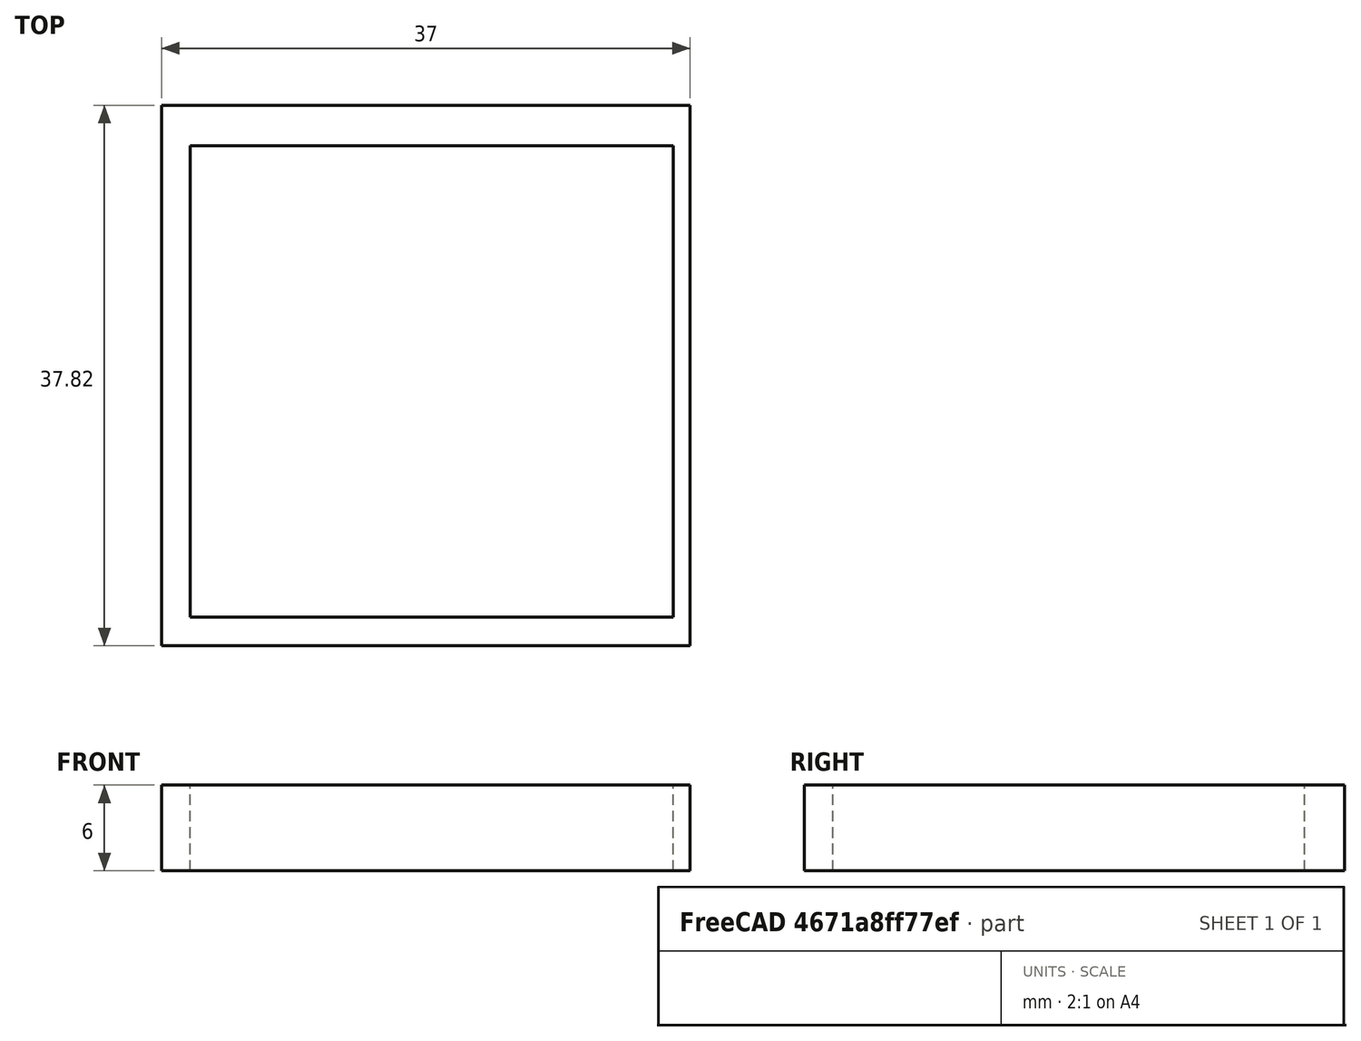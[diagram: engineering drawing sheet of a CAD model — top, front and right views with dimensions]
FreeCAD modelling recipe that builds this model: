
FCSTD DOCUMENT  (FreeCAD 0.18.4R)
Label: midi_pad_square_mount_2
License: All rights reserved
LicenseURL: http://en.wikipedia.org/wiki/All_rights_reserved
objects: Path::FeaturePython×13, Sketcher::SketchObject×8, App::MeasureDistance×5, Mesh::FeaturePython×5, PartDesign::Pocket×4, Part::FeaturePython×4, PartDesign::Hole×2, App::FeaturePython×2, App::DocumentObjectGroup×2, Path::FeatureCompoundPython×2, PartDesign::Pad×1, Spreadsheet::Sheet×1, Image::ImagePlane×1, PartDesign::Fillet×1, PartDesign::Body×1
note: 32 computed .brp shape members not serialized (recipe doc carries the construction recipe); baked Part::Feature solids carry a one-line shape summary decoded from their .brp

FEATURE [Sketcher::SketchObject] Sketch  label="base"
  MapMode = 5
  Support = -> [XY_Plane]
  sketch-geometry (4):
    g0: LineSegment StartX=-11.5 StartY=11.91 StartZ=0 EndX=11.5 EndY=11.91 EndZ=0
    g1: LineSegment StartX=11.5 StartY=11.91 StartZ=0 EndX=11.5 EndY=-11.91 EndZ=0
    g2: LineSegment StartX=11.5 StartY=-11.91 StartZ=0 EndX=-11.5 EndY=-11.91 EndZ=0
    g3: LineSegment StartX=-11.5 StartY=-11.91 StartZ=0 EndX=-11.5 EndY=11.91 EndZ=0
  constraints (11):
    c: Coincident(g0,g1)
    c: Coincident(g1,g2)
    c: Coincident(g2,g3)
    c: Coincident(g3,g0)
    c: Horizontal(g0)
    c: Horizontal(g2)
    c: Vertical(g1)
    c: Vertical(g3)
    c: DistanceY(g1,g1) = 23.82
    c: DistanceX(g0,g0) = 23
    c: Symmetric(g0,g2,g-1)
FEATURE [PartDesign::Pad] Pad  label="basePlate"
  Length = 6
  Length2 = 100
  Profile = -> Sketch
  Type = 0
  expr: Length = parameters.separator + parameters.balero_h
FEATURE [Spreadsheet::Sheet] Spreadsheet  label="parameters"
  cells = A1=balero_R; B1(balero_R)=7.95; A2=balero_r; B2(balero_r)=2.35; A3=balero_h; B3(balero_h)=5; A4=pin_w; B4(pin_w)=10.2; A5=r_w; B5(r_w)=10; A6=cutout_d; B6(cutout_d)=1.7; A7=wall_thickness; B7(wall_thickness)=3.5; A8=separator; B8(separator)=1; A9=center hole D; B9(center_hole_D)=3; A10=screw Head D; B10(screwHeadD)=5.5; A11=screw D; B11(screwMountD)=3.5; A12=OpToolHeightStep; B12(OpToolHeightStep)=0.25
FEATURE [Image::ImagePlane] ImagePlane
  Placement = pos=(99.4,-140.15,0) rot=(0,0,1;0rad)
  XSize = 222.326
  YSize = 305.698
FEATURE [App::MeasureDistance] Distance  label="Distance: left to center"
  Distance = 11.5
  P1 = (-11.5,0,0)
  P2 = (0,0,0)
FEATURE [App::MeasureDistance] Distance001  label="Distance: right to center"
  Distance = 11.5
  P1 = (11.5,0,0)
  P2 = (0,0,0)
FEATURE [App::MeasureDistance] Distance002  label="Distance: bottom to center"
  Distance = 7.58
  P1 = (0,-7.58,0)
  P2 = (0,0,0)
FEATURE [App::MeasureDistance] Distance003  label="Distance: up to center"
  Distance = 7.56
  P1 = (0,7.56,0)
  P2 = (0,0,0)
FEATURE [Sketcher::SketchObject] Sketch001  label="balero+wall"
  MapMode = 5
  Placement = pos=(0,0,6) rot=(0,0,1;0rad)
  Support = -> [Pad]
  expr: Constraints[1] = parameters.balero_R + parameters.wall_thickness
  sketch-geometry (5):
    g0: Circle CenterX=0 CenterY=0 CenterZ=0 NormalX=0 NormalY=0 NormalZ=1 AngleXU=0 Radius=11.45
    g1: LineSegment StartX=-20 StartY=20 StartZ=0 EndX=20 EndY=20 EndZ=0
    g2: LineSegment StartX=20 StartY=20 StartZ=0 EndX=20 EndY=-20 EndZ=0
    g3: LineSegment StartX=20 StartY=-20 StartZ=0 EndX=-20 EndY=-20 EndZ=0
    g4: LineSegment StartX=-20 StartY=-20 StartZ=0 EndX=-20 EndY=20 EndZ=0
  constraints (13):
    c: Coincident(g0,g-1)
    c: Radius(g0) = 11.45
    c: Coincident(g1,g2)
    c: Coincident(g2,g3)
    c: Coincident(g3,g4)
    c: Coincident(g4,g1)
    c: Horizontal(g1)
    c: Horizontal(g3)
    c: Vertical(g2)
    c: Vertical(g4)
    c: DistanceX(g1,g1) = 40
    c: DistanceY(g4,g4) = 40
    c: Symmetric(g1,g3,g0)
FEATURE [PartDesign::Fillet] Fillet
  Base = -> Pad [Edge5,Edge8,Edge2,Edge1]
  BaseFeature = -> Pad
  Radius = 3
FEATURE [Sketcher::SketchObject] Sketch003  label="pin cutout shape"
  MapMode = 5
  Placement = pos=(0,0,0) rot=(1,0,0;3.14159rad)
  expr: Constraints[14] = 3.5 / 2
  sketch-geometry (8):
    g0: ArcOfCircle CenterX=4 CenterY=-6.75 CenterZ=0 NormalX=0 NormalY=0 NormalZ=1 AngleXU=0 Radius=1.75 StartAngle=4.71239 EndAngle=7.85398
    g1: ArcOfCircle CenterX=-3.12 CenterY=-6.75 CenterZ=0 NormalX=0 NormalY=0 NormalZ=1 AngleXU=0 Radius=1.75 StartAngle=1.5708 EndAngle=4.71239
    g2: LineSegment StartX=4 StartY=-5 StartZ=0 EndX=-3.12 EndY=-5 EndZ=0
    g3: LineSegment StartX=4 StartY=-8.5 StartZ=0 EndX=-3.12 EndY=-8.5 EndZ=0
    g4: ArcOfCircle CenterX=2.38 CenterY=6.76 CenterZ=0 NormalX=0 NormalY=0 NormalZ=1 AngleXU=0 Radius=1.75 StartAngle=4.71239 EndAngle=7.85398
    g5: ArcOfCircle CenterX=-2.34 CenterY=6.76 CenterZ=0 NormalX=0 NormalY=0 NormalZ=1 AngleXU=0 Radius=1.75 StartAngle=1.5708 EndAngle=4.71239
    g6: LineSegment StartX=2.38 StartY=8.51 StartZ=0 EndX=-2.34 EndY=8.51 EndZ=0
    g7: LineSegment StartX=2.38 StartY=5.01 StartZ=0 EndX=-2.34 EndY=5.01 EndZ=0
  constraints (20):
    c: Tangent(g0,g3) = 1.5708
    c: Tangent(g0,g2) = -1.5708
    c: Tangent(g2,g1) = -1.5708
    c: Tangent(g3,g1) = 1.5708
    c: Horizontal(g2)
    c: Tangent(g4,g7) = 1.5708
    c: Tangent(g4,g6) = -1.5708
    c: Tangent(g6,g5) = -1.5708
    c: Tangent(g7,g5) = 1.5708
    c: Horizontal(g6)
    c: DistanceX(g5,g-1) = 2.34
    c: DistanceX(g-1,g0) = 4
    c: DistanceX(g1,g-1) = 3.12
    c: DistanceX(g-1,g4) = 2.38
    c: Radius(g5) = 1.75
    c: Equal(g5,g4)
    c: Equal(g5,g1)
    c: Equal(g5,g0)
    c: DistanceY(g-1,g5) = 6.76
    c: DistanceY(g1,g-1) = 6.75
FEATURE [PartDesign::Pocket] Pocket  label="pin pocket"
  BaseFeature = -> Fillet
  Length = 1
  Length2 = 100
  Profile = -> Sketch003
  Type = 0
  expr: Length = parameters.separator
FEATURE [PartDesign::Pocket] Pocket001  label="outer pocket"
  BaseFeature = -> Pocket
  Length = 5
  Length2 = 100
  Profile = -> Sketch001
  Type = 0
  expr: Length = parameters.balero_h
FEATURE [Sketcher::SketchObject] Sketch004  label="baleroR"
  MapMode = 5
  Placement = pos=(0,0,1) rot=(1,0,0;3.14159rad)
  Support = -> [Pocket001]
  expr: Constraints[0] = parameters.balero_R
  sketch-geometry (1):
    g0: Circle CenterX=-0.007428 CenterY=-0.004957 CenterZ=0 NormalX=0 NormalY=0 NormalZ=1 AngleXU=0 Radius=7.95
  constraints (1):
    c: Radius(g0) = 7.95
FEATURE [PartDesign::Pocket] Pocket002  label="balero pocket001"
  BaseFeature = -> Pocket001
  Length = 5
  Length2 = 100
  Profile = -> Sketch004
  Type = 0
  expr: Length = parameters.balero_h
FEATURE [Sketcher::SketchObject] Sketch006
  MapMode = 5
  Placement = pos=(0,0,6) rot=(0,0,1;0rad)
  expr: Constraints[0] = parameters.screwMountD
  sketch-geometry (4):
    g0: Circle CenterX=-8.25 CenterY=8.25 CenterZ=0 NormalX=0 NormalY=0 NormalZ=1 AngleXU=0 Radius=1.75
    g1: Circle CenterX=8.25 CenterY=8.25 CenterZ=0 NormalX=0 NormalY=0 NormalZ=1 AngleXU=0 Radius=1.75
    g2: Circle CenterX=8.25 CenterY=-8.25 CenterZ=0 NormalX=0 NormalY=0 NormalZ=1 AngleXU=0 Radius=1.75
    g3: Circle CenterX=-8.25 CenterY=-8.25 CenterZ=0 NormalX=0 NormalY=0 NormalZ=1 AngleXU=0 Radius=1.75
  constraints (9):
    c: Diameter(g0) = 3.5
    c: Equal(g0,g1)
    c: Equal(g0,g2)
    c: Equal(g0,g3)
    c: Symmetric(g1,g3,g-1)
    c: Symmetric(g2,g0,g-1)
    c: Symmetric(g2,g1,g-1)
    c: Distance(g2,g-1) = 8.25
    c: Distance(g2,g-2) = 8.25
FEATURE [Sketcher::SketchObject] Sketch007
  MapMode = 5
  Placement = pos=(0,0,6) rot=(0,0,1;0rad)
  expr: Constraints[4] = parameters.screwHeadD
  sketch-geometry (4):
    g0: Circle CenterX=-8.2937 CenterY=8.18875 CenterZ=0 NormalX=0 NormalY=0 NormalZ=1 AngleXU=0 Radius=2.75
    g1: Circle CenterX=8.2937 CenterY=8.18875 CenterZ=0 NormalX=0 NormalY=0 NormalZ=1 AngleXU=0 Radius=2.75
    g2: Circle CenterX=8.2937 CenterY=-8.18875 CenterZ=0 NormalX=0 NormalY=0 NormalZ=1 AngleXU=0 Radius=2.75
    g3: Circle CenterX=-8.2937 CenterY=-8.18875 CenterZ=0 NormalX=0 NormalY=0 NormalZ=1 AngleXU=0 Radius=2.75
  constraints (8):
    c: Symmetric(g1,g0,g-2)
    c: Symmetric(g1,g2,g-1)
    c: Symmetric(g2,g0,g-1)
    c: Symmetric(g3,g1,g-1)
    c: Diameter(g3) = 5.5
    c: Equal(g3,g0)
    c: Equal(g3,g1)
    c: Equal(g3,g2)
FEATURE [PartDesign::Hole] Hole
  BaseFeature = -> Pocket002
  Depth = 25
  DepthType = 1
  Diameter = 3.5
  DrillPoint = 0
  DrillPointAngle = 118
  HoleCutCountersinkAngle = 90
  HoleCutDepth = 0
  HoleCutDiameter = 0
  HoleCutType = 0
  ModelActualThread = false
  Profile = -> Sketch006
  Tapered = false
  TaperedAngle = 90
  ThreadAngle = 0
  ThreadClass = 0
  ThreadCutOffInner = 0
  ThreadCutOffOuter = 0
  ThreadDirection = 0
  ThreadFit = 0
  ThreadPitch = 0
  ThreadSize = 0
  ThreadType = 0
  Threaded = false
  expr: Diameter = parameters.screwMountD
FEATURE [PartDesign::Pocket] Pocket004  label="screw head pockets"
  BaseFeature = -> Hole
  Length = 5
  Length2 = 100
  Profile = -> Sketch007
  Type = 0
  expr: Length = parameters.balero_h
FEATURE [Sketcher::SketchObject] Sketch008
  MapMode = 5
  Placement = pos=(0,0,6) rot=(0,0,1;0rad)
  Support = -> [Pad]
  expr: Constraints[1] = parameters.center_hole_D
  sketch-geometry (1):
    g0: Circle CenterX=0 CenterY=0 CenterZ=0 NormalX=0 NormalY=0 NormalZ=1 AngleXU=0 Radius=1.5
  constraints (2):
    c: Coincident(g0,g-1)
    c: Diameter(g0) = 3
FEATURE [PartDesign::Hole] Hole001
  BaseFeature = -> Pocket004
  Depth = 25
  DepthType = 0
  Diameter = 3
  DrillPoint = 0
  DrillPointAngle = 118
  HoleCutCountersinkAngle = 90
  HoleCutDepth = 0
  HoleCutDiameter = 0
  HoleCutType = 0
  ModelActualThread = false
  Profile = -> Sketch008
  Tapered = false
  TaperedAngle = 90
  ThreadAngle = 0
  ThreadClass = 0
  ThreadCutOffInner = 0
  ThreadCutOffOuter = 0
  ThreadDirection = 0
  ThreadFit = 0
  ThreadPitch = 0
  ThreadSize = 0
  ThreadType = 0
  Threaded = false
  expr: Diameter = parameters.center_hole_D
FEATURE [App::FeaturePython] SetupSheet  # Path/CAM operation (typed FeaturePython)
  ClearanceHeightExpression = OpStockZMax+SetupSheet.ClearanceHeightOffset
  ClearanceHeightOffset = 3
  FinalDepthExpression = OpFinalDepth
  HorizRapid = 0
  SafeHeightExpression = OpStockZMax+SetupSheet.SafeHeightOffset
  SafeHeightOffset = 2
  StartDepthExpression = OpStartDepth
  StepDownExpression = OpToolDiameter
  VertRapid = 0
FEATURE [Path::FeaturePython] T2__Mill_Bit_standard  label="T2: Mill Bit standard"  # Path/CAM operation (typed FeaturePython)
  HorizFeed = 1
  HorizRapid = 0
  SpindleDir = 0
  SpindleSpeed = 12000
  ToolNumber = 2
  VertFeed = 1
  VertRapid = 0
  expr: HorizRapid = SetupSheet.HorizRapid
  expr: VertRapid = SetupSheet.VertRapid
FEATURE [Path::FeaturePython] Contour  # Path/CAM operation (typed FeaturePython)
  Active = true
  AreaParams:
    Tolerance = 1e-07
    FitArcs = True
    Simplify = False
    CleanDistance = 0.0
    Accuracy = 0.01
    Unit = 1.0
    MinArcPoints = 4
    MaxArcPoints = 100
    ClipperScale = 10000000.0
    Fill = 0
    Coplanar = 2
    Reorient = True
    Outline = False
    Explode = False
    OpenMode = 0
    Deflection = 0.01
    SubjectFill = 0
    ClipFill = 0
    Offset = 1.55
    ExtraPass = 0
    Stepover = 0.0
    LastStepover = 0.0
    JoinType = 0
    EndType = 0
    MiterLimit = 2.0
    RoundPrecision = 0.0
    PocketMode = 0
    ToolRadius = 1.0
    PocketExtraOffset = 0.0
    PocketStepover = 0.0
    PocketLastStepover = 0.0
    FromCenter = False
    Angle = 45.0
    AngleShift = 0.0
    Shift = 0.0
    Thicken = False
    SectionCount = -1
    Stepdown = 1.0
    SectionOffset = 0.0
    SectionTolerance = 1e-06
    SectionMode = 2
    Project = False
  ClearanceHeight = 9
  Direction = 0
  FinalDepth = 0
  JoinType = 0
  MiterLimit = 0.1
  OffsetExtra = 0
  OpFinalDepth = 0
  OpStartDepth = 6
  OpStockZMax = 6
  OpStockZMin = 0
  OpToolDiameter = 3.1
  PathParams = {'orientation': 1, 'feedrate': 1.0, 'feedrate_v': 1.0, 'verbose': True, 'resume_height': 8.0, 'retraction': 9.0, 'return_end': True, 'preamble': False}
  SafeHeight = 8
  Side = 0
  StartDepth = 6
  StartPoint = (0,0,0)
  StepDown = 0.25
  ToolController = -> T2__Mill_Bit_standard
  UseComp = true
  UseStartPoint = false
  expr: StepDown = parameters.OpToolHeightStep
  expr: ClearanceHeight = OpStockZMax + SetupSheet.ClearanceHeightOffset
  expr: SafeHeight = OpStockZMax + SetupSheet.SafeHeightOffset
  expr: FinalDepth = OpFinalDepth
  expr: StartDepth = OpStartDepth
FEATURE [Mesh::FeaturePython] CutMaterial  # WARN: FeaturePython — macro-defined, semantics opaque (R4)
FEATURE [Mesh::FeaturePython] CutMaterial001  # WARN: FeaturePython — macro-defined, semantics opaque (R4)
FEATURE [Sketcher::SketchObject] Sketch009
  MapMode = 5
  Placement = pos=(0,0,0) rot=(1,0,0;3.14159rad)
  Support = -> [Pad]
  sketch-geometry (4):
    g0: LineSegment StartX=30 StartY=-30 StartZ=0 EndX=-30 EndY=-30 EndZ=0
    g1: LineSegment StartX=-30 StartY=-30 StartZ=0 EndX=-30 EndY=30 EndZ=0
    g2: LineSegment StartX=-30 StartY=30 StartZ=0 EndX=30 EndY=30 EndZ=0
    g3: LineSegment StartX=30 StartY=30 StartZ=0 EndX=30 EndY=-30 EndZ=0
  constraints (11):
    c: Coincident(g0,g1)
    c: Coincident(g1,g2)
    c: Coincident(g2,g3)
    c: Coincident(g3,g0)
    c: Horizontal(g0)
    c: Horizontal(g2)
    c: Vertical(g1)
    c: Vertical(g3)
    c: Symmetric(g0,g2,g-1)
    c: DistanceX(g0,g0) = 60
    c: DistanceY(g3,g3) = 60
FEATURE [PartDesign::Body] Body
  Group = -> [Sketch,Pad,Fillet,Sketch003,Pocket,Sketch001,Pocket001,Sketch004,Pocket002,Sketch006,Sketch007,Hole,Pocket004,Sketch008,Hole001,Sketch009]
  Origin = -> Origin
  Tip = -> Hole001
FEATURE [Part::FeaturePython] Clone  label="Model-Body"  # Draft clone (typed FeaturePython)
  AttacherType = Attacher::AttachEngine3D
  Fuse = false
  Objects = -> [Body]
  PathResource = Model
  Scale = (1,1,1)
FEATURE [App::DocumentObjectGroup] Model
  Group = -> [Clone]
FEATURE [Part::FeaturePython] Stock  # WARN: FeaturePython — macro-defined, semantics opaque (R4)
  Base = -> Model
  ExtXneg = 7
  ExtXpos = 7
  ExtYneg = 7
  ExtYpos = 7
  ExtZneg = 0
  ExtZpos = 0
  Placement = pos=(-11.5,-11.91,0) rot=(0,0,1;0rad)
  StockType = FromBase
FEATURE [Path::FeaturePython] Drilling  # Path/CAM operation (typed FeaturePython)
  Active = true
  AddTipLength = false
  Base = -> [Clone]
  ClearanceHeight = 9
  DwellEnabled = false
  DwellTime = 0
  FinalDepth = 0
  OpFinalDepth = 0
  OpStartDepth = 6
  OpStockZMax = 6
  OpStockZMin = 0
  OpToolDiameter = 3.1
  PeckDepth = 0.5
  PeckEnabled = true
  RetractHeight = 2
  ReturnLevel = 0
  SafeHeight = 8
  StartDepth = 6
  ToolController = -> T2__Mill_Bit_standard
  expr: ClearanceHeight = OpStockZMax + SetupSheet.ClearanceHeightOffset
  expr: SafeHeight = OpStockZMax + SetupSheet.SafeHeightOffset
  expr: FinalDepth = OpFinalDepth
  expr: StartDepth = OpStartDepth
FEATURE [Path::FeaturePython] Drilling001  # Path/CAM operation (typed FeaturePython)
  Active = true
  AddTipLength = false
  Base = -> [Clone]
  ClearanceHeight = 9
  DwellEnabled = false
  DwellTime = 0
  FinalDepth = 0
  OpFinalDepth = 0
  OpStartDepth = 6
  OpStockZMax = 6
  OpStockZMin = 0
  OpToolDiameter = 3.1
  PeckDepth = 0.5
  PeckEnabled = true
  RetractHeight = 2
  ReturnLevel = 0
  SafeHeight = 8
  StartDepth = 6
  ToolController = -> T2__Mill_Bit_standard
  expr: ClearanceHeight = OpStockZMax + SetupSheet.ClearanceHeightOffset
  expr: SafeHeight = OpStockZMax + SetupSheet.SafeHeightOffset
  expr: FinalDepth = OpFinalDepth
  expr: StartDepth = OpStartDepth
FEATURE [Path::FeaturePython] Pocket_3D002  # Path/CAM operation (typed FeaturePython)
  Active = true
  AreaParams:
    Tolerance = 1e-07
    FitArcs = True
    Simplify = False
    CleanDistance = 0.0
    Accuracy = 0.01
    Unit = 1.0
    MinArcPoints = 4
    MaxArcPoints = 100
    ClipperScale = 10000000.0
    Fill = 0
    Coplanar = 0
    Reorient = True
    Outline = False
    Explode = False
    OpenMode = 0
    Deflection = 0.01
    SubjectFill = 0
    ClipFill = 0
    Offset = 0.0
    ExtraPass = 0
    Stepover = 0.0
    LastStepover = 0.0
    JoinType = 0
    EndType = 0
    MiterLimit = 2.0
    RoundPrecision = 0.0
    PocketMode = 4
    ToolRadius = 1.55
    PocketExtraOffset = 0.0
    PocketStepover = 1.2400000000000002
    PocketLastStepover = 0.0
    FromCenter = True
    Angle = 135.0
    AngleShift = 0.0
    Shift = 0.0
    Thicken = False
    SectionCount = -1
    Stepdown = 1.0
    SectionOffset = 0.0
    SectionTolerance = 1e-06
    SectionMode = 2
    Project = False
  Base = -> [Clone]
  ClearanceHeight = 9
  CutMode = 0
  ExtraOffset = 0
  FinalDepth = 1
  FinishDepth = 0
  KeepToolDown = false
  MinTravel = false
  OffsetPattern = 3
  OpFinalDepth = 1
  OpStartDepth = 6
  OpStockZMax = 6
  OpStockZMin = 0
  OpToolDiameter = 3.1
  PathParams = {'orientation': 1, 'feedrate': 1.0, 'feedrate_v': 1.0, 'verbose': True, 'resume_height': 8.0, 'retraction': 9.0, 'return_end': True, 'preamble': False}
  SafeHeight = 8
  StartAt = 0
  StartDepth = 6
  StartPoint = (0,0,0)
  StepDown = 0.25
  StepOver = 40
  ToolController = -> T2__Mill_Bit_standard
  UseStartPoint = false
  ZigZagAngle = 135
  expr: StepDown = parameters.OpToolHeightStep
  expr: ClearanceHeight = OpStockZMax + SetupSheet.ClearanceHeightOffset
  expr: SafeHeight = OpStockZMax + SetupSheet.SafeHeightOffset
  expr: FinalDepth = OpFinalDepth
  expr: StartDepth = OpStartDepth
FEATURE [Path::FeaturePython] Profile_Faces  # Path/CAM operation (typed FeaturePython)
  Active = true
  AreaParams:
    Tolerance = 1e-07
    FitArcs = True
    Simplify = False
    CleanDistance = 0.0
    Accuracy = 0.01
    Unit = 1.0
    MinArcPoints = 4
    MaxArcPoints = 100
    ClipperScale = 10000000.0
    Fill = 0
    Coplanar = 0
    Reorient = True
    Outline = False
    Explode = False
    OpenMode = 0
    Deflection = 0.01
    SubjectFill = 0
    ClipFill = 0
    Offset = 1.55
    ExtraPass = 0
    Stepover = 0.0
    LastStepover = 0.0
    JoinType = 0
    EndType = 0
    MiterLimit = 2.0
    RoundPrecision = 0.0
    PocketMode = 0
    ToolRadius = 1.0
    PocketExtraOffset = 0.0
    PocketStepover = 0.0
    PocketLastStepover = 0.0
    FromCenter = False
    Angle = 45.0
    AngleShift = 0.0
    Shift = 0.0
    Thicken = False
    SectionCount = -1
    Stepdown = 1.0
    SectionOffset = 0.0
    SectionTolerance = 1e-06
    SectionMode = 2
    Project = False
  Base = -> [Clone]
  ClearanceHeight = 9
  Direction = 0
  FinalDepth = 1
  JoinType = 0
  MiterLimit = 0.1
  OffsetExtra = 0
  OpFinalDepth = 1
  OpStartDepth = 6
  OpStockZMax = 6
  OpStockZMin = 0
  OpToolDiameter = 3.1
  PathParams = {'orientation': 0, 'feedrate': 1.0, 'feedrate_v': 1.0, 'verbose': True, 'resume_height': 8.0, 'retraction': 9.0, 'return_end': True, 'preamble': False}
  SafeHeight = 8
  Side = 1
  StartDepth = 6
  StartPoint = (0,0,0)
  StepDown = 0.25
  ToolController = -> T2__Mill_Bit_standard
  UseComp = true
  UseStartPoint = false
  processCircles = true
  processHoles = true
  processPerimeter = false
  expr: StepDown = parameters.OpToolHeightStep
  expr: ClearanceHeight = OpStockZMax + SetupSheet.ClearanceHeightOffset
  expr: SafeHeight = OpStockZMax + SetupSheet.SafeHeightOffset
  expr: FinalDepth = OpFinalDepth
  expr: StartDepth = OpStartDepth
FEATURE [Mesh::FeaturePython] CutMaterial002  # WARN: FeaturePython — macro-defined, semantics opaque (R4)
FEATURE [Mesh::FeaturePython] CutMaterial003  # WARN: FeaturePython — macro-defined, semantics opaque (R4)
FEATURE [Path::FeaturePython] TagDressup  # Path/CAM operation (typed FeaturePython)
  Angle = 90
  Base = -> Contour
  Height = 0.5
  Positions = (4) [(13.0476,0.0608057,0),(0.0608058,-13.4576,0),(-13.0476,-0.0608057,0),(-0.0608058,13.4576,0)]
  Radius = 0
  SegmentationFactor = 50
  Width = 2
FEATURE [Path::FeatureCompoundPython] Operations  # Path/CAM operation (typed FeaturePython)
  Group = -> [Drilling,Drilling001,Pocket_3D002,Profile_Faces,TagDressup]
  UsePlacements = false
FEATURE [Path::FeaturePython] Job  # Path/CAM operation (typed FeaturePython)
  GeometryTolerance = 0.01
  Model = -> Model
  Operations = -> Operations
  PostProcessor = 4
  PostProcessorOutputFile = <userpath>/FreeCAD/Projects/midi_pad/0_mid_pad_square_top.gcode
  SetupSheet = -> SetupSheet
  Stock = -> Stock
  ToolController = -> [T2__Mill_Bit_standard]
FEATURE [App::MeasureDistance] Distance004  label="Distance: 23,56 mm"
  Distance = 6
  P1 = (0,0,6)
  P2 = (0,0,0)
FEATURE [App::FeaturePython] SetupSheet001  # Path/CAM operation (typed FeaturePython)
  ClearanceHeightExpression = OpStockZMax+SetupSheet001.ClearanceHeightOffset
  ClearanceHeightOffset = 5
  FinalDepthExpression = OpFinalDepth
  HorizRapid = 0
  SafeHeightExpression = OpStockZMax+SetupSheet001.SafeHeightOffset
  SafeHeightOffset = 3
  StartDepthExpression = OpStartDepth
  StepDownExpression = OpToolDiameter
  VertRapid = 0
FEATURE [Part::FeaturePython] Clone001  label="Model-Body001"  # Draft clone (typed FeaturePython)
  AttacherType = Attacher::AttachEngine3D
  Fuse = false
  Objects = -> [Body]
  PathResource = Model
  Placement = pos=(-1.8e-15,1.8e-15,6) rot=(0.707107,0.707107,0;3.14159rad)
  Scale = (1,1,1)
FEATURE [App::DocumentObjectGroup] Model001
  Group = -> [Clone001]
FEATURE [Part::FeaturePython] Stock001  # WARN: FeaturePython — macro-defined, semantics opaque (R4)
  Base = -> Model001
  ExtXneg = 5
  ExtXpos = 5
  ExtYneg = 5
  ExtYpos = 5
  ExtZneg = 0
  ExtZpos = 0
  Placement = pos=(-11.5,-11.91,0) rot=(0,0,1;0rad)
  StockType = FromBase
FEATURE [Path::FeaturePython] T2__Mill_Bit_standard001  label="T2: Mill Bit standard001"  # Path/CAM operation (typed FeaturePython)
  HorizFeed = 6
  HorizRapid = 0
  SpindleDir = 0
  SpindleSpeed = 12000
  ToolNumber = 2
  VertFeed = 6
  VertRapid = 0
  expr: HorizRapid = SetupSheet001.HorizRapid
  expr: VertRapid = SetupSheet001.VertRapid
FEATURE [Path::FeaturePython] T3__Dummy1mmMill  label="T3: Dummy1mmMill"  # Path/CAM operation (typed FeaturePython)
  HorizFeed = 0
  HorizRapid = 0
  SpindleDir = 0
  SpindleSpeed = 0
  ToolNumber = 3
  VertFeed = 0
  VertRapid = 0
  expr: HorizRapid = SetupSheet001.HorizRapid
  expr: VertRapid = SetupSheet001.VertRapid
FEATURE [Path::FeaturePython] Profile_Edges  # Path/CAM operation (typed FeaturePython)
  Active = true
  AreaParams:
    Tolerance = 1e-07
    FitArcs = True
    Simplify = False
    CleanDistance = 0.0
    Accuracy = 0.01
    Unit = 1.0
    MinArcPoints = 4
    MaxArcPoints = 100
    ClipperScale = 10000000.0
    Fill = 0
    Coplanar = 0
    Reorient = True
    Outline = False
    Explode = False
    OpenMode = 0
    Deflection = 0.01
    SubjectFill = 0
    ClipFill = 0
    Offset = -1.55
    ExtraPass = 0
    Stepover = 0.0
    LastStepover = 0.0
    JoinType = 0
    EndType = 0
    MiterLimit = 2.0
    RoundPrecision = 0.0
    PocketMode = 0
    ToolRadius = 1.0
    PocketExtraOffset = 0.0
    PocketStepover = 0.0
    PocketLastStepover = 0.0
    FromCenter = False
    Angle = 45.0
    AngleShift = 0.0
    Shift = 0.0
    Thicken = False
    SectionCount = -1
    Stepdown = 1.0
    SectionOffset = 0.0
    SectionTolerance = 1e-06
    SectionMode = 2
    Project = False
  Base = -> [Clone001]
  ClearanceHeight = 11
  Direction = 0
  FinalDepth = 5
  JoinType = 0
  MiterLimit = 0.1
  OffsetExtra = 0
  OpFinalDepth = 5
  OpStartDepth = 6
  OpStockZMax = 6
  OpStockZMin = 0
  OpToolDiameter = 3.1
  PathParams = {'orientation': 1, 'feedrate': 6.0, 'feedrate_v': 6.0, 'verbose': True, 'resume_height': 9.000000000000005, 'retraction': 11.000000000000005, 'return_end': True, 'preamble': False}
  SafeHeight = 9
  Side = 1
  StartDepth = 6
  StartPoint = (0,0,0)
  StepDown = 3.1
  ToolController = -> T2__Mill_Bit_standard001
  UseComp = true
  UseStartPoint = false
  expr: ClearanceHeight = OpStockZMax + SetupSheet001.ClearanceHeightOffset
  expr: SafeHeight = OpStockZMax + SetupSheet001.SafeHeightOffset
  expr: StepDown = OpToolDiameter
  expr: FinalDepth = OpFinalDepth
  expr: StartDepth = OpStartDepth
FEATURE [Path::FeaturePython] Drilling002  # Path/CAM operation (typed FeaturePython)
  Active = true
  AddTipLength = false
  Base = -> [Clone001]
  ClearanceHeight = 11
  DwellEnabled = false
  DwellTime = 0
  FinalDepth = 5
  OpFinalDepth = 5
  OpStartDepth = 6
  OpStockZMax = 6
  OpStockZMin = 0
  OpToolDiameter = 3.1
  PeckDepth = 0
  PeckEnabled = true
  RetractHeight = 10
  ReturnLevel = 0
  SafeHeight = 9
  StartDepth = 6
  ToolController = -> T2__Mill_Bit_standard001
  expr: ClearanceHeight = OpStockZMax + SetupSheet001.ClearanceHeightOffset
  expr: SafeHeight = OpStockZMax + SetupSheet001.SafeHeightOffset
  expr: FinalDepth = OpFinalDepth
  expr: StartDepth = OpStartDepth
FEATURE [Path::FeatureCompoundPython] Operations001  # Path/CAM operation (typed FeaturePython)
  Group = -> [Profile_Edges,Drilling002]
  UsePlacements = false
FEATURE [Path::FeaturePython] Job001  # Path/CAM operation (typed FeaturePython)
  GeometryTolerance = 0.01
  Model = -> Model001
  Operations = -> Operations001
  PostProcessor = 4
  PostProcessorOutputFile = <userpath>/FreeCAD/Projects/midi_pad/0_midi_pad_square_bottom.gcode
  SetupSheet = -> SetupSheet001
  Stock = -> Stock001
  ToolController = -> [T2__Mill_Bit_standard001,T3__Dummy1mmMill]
FEATURE [Mesh::FeaturePython] CutMaterial004  # WARN: FeaturePython — macro-defined, semantics opaque (R4)
